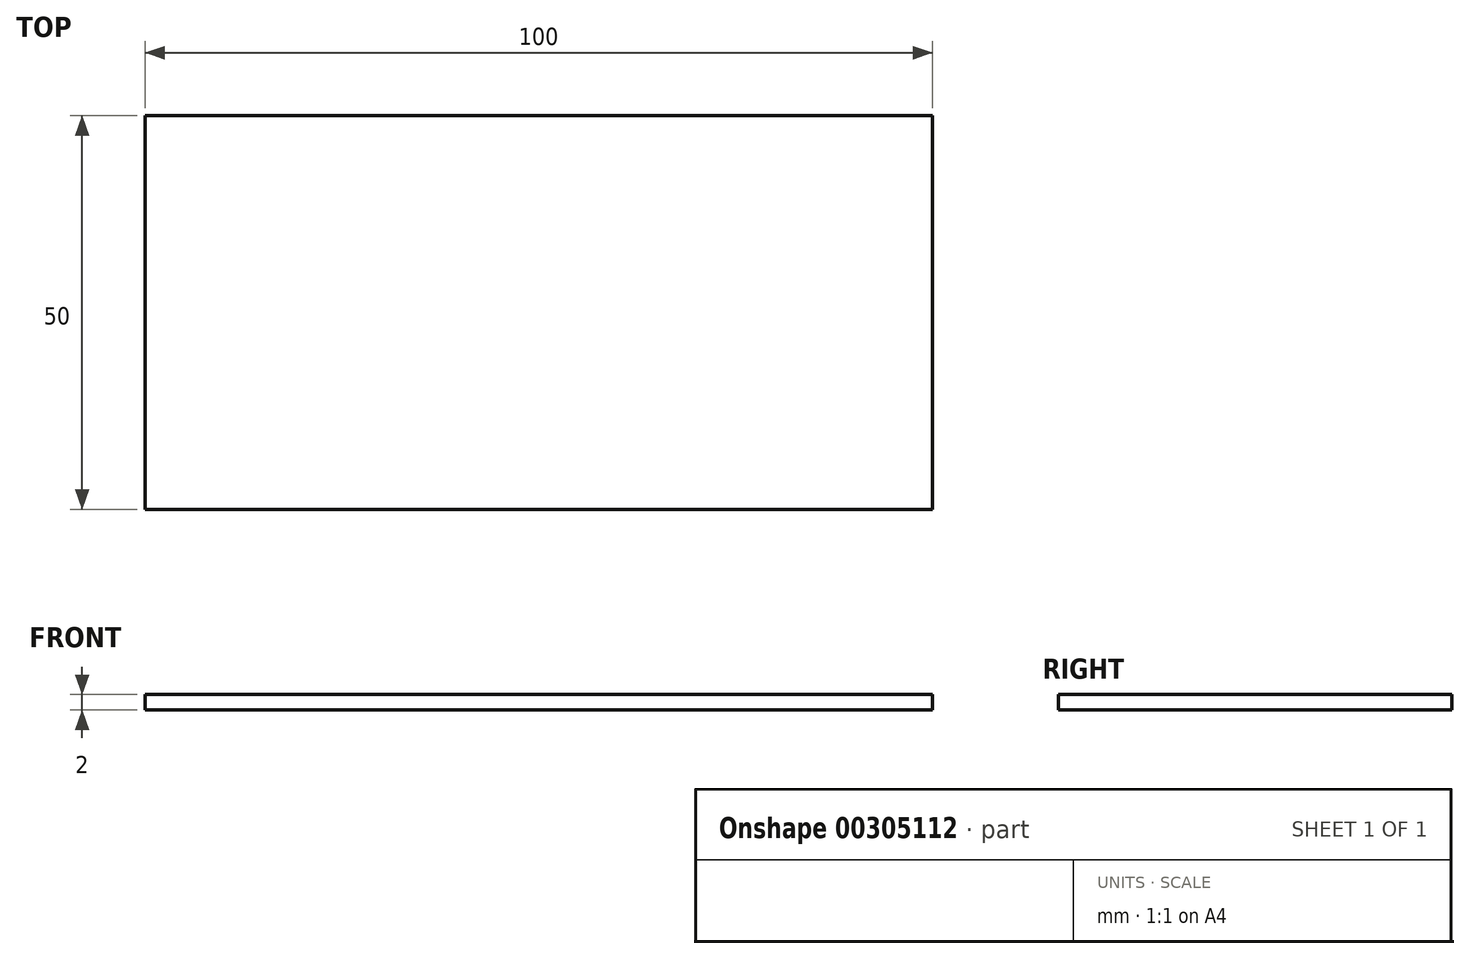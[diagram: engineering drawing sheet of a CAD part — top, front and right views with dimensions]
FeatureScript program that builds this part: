
annotation { "Feature Type Name" : "Feature", "Feature Type Description" : "" }
export const myFeature = defineFeature(function(context is Context, id is Id, definition is map)
    precondition{}
    {
        {
            var Q0;
            Q0=qCreatedBy(makeId("Top.planeOp"),FACE);
            var sketch = newSketch(context, id + "F0", { "sketchPlane" : qUnion([Q0])});
            skLineSegment(sketch, "E0.bottom", {"start": v(0, 0) * mm, "end": v(-100, 0) * mm});
            skLineSegment(sketch, "E0.top", {"start": v(0, 50) * mm, "end": v(-100, 50) * mm});
            skLineSegment(sketch, "E0.left", {"start": v(0, 0) * mm, "end": v(0, 50) * mm});
            skLineSegment(sketch, "E0.right", {"start": v(-100, 0) * mm, "end": v(-100, 50) * mm});
            skSolve(sketch);
        }
        {
            var Q0;
            Q0=makeQuery(id+"F0.imprint","IMPRINT",FACE,{"disambiguationData":[TD([[makeQuery(id+"F0.imprint","IMPRINT",EDGE,{"derivedFrom":sQuery(id+"F0.wireOp",EDGE,"E0.bottom")}),-1.0]])]});
            extrude(context, id + "F1", {"entities" : qUnion([Q0]), "depth" : 2 * mm});
        }
    });
